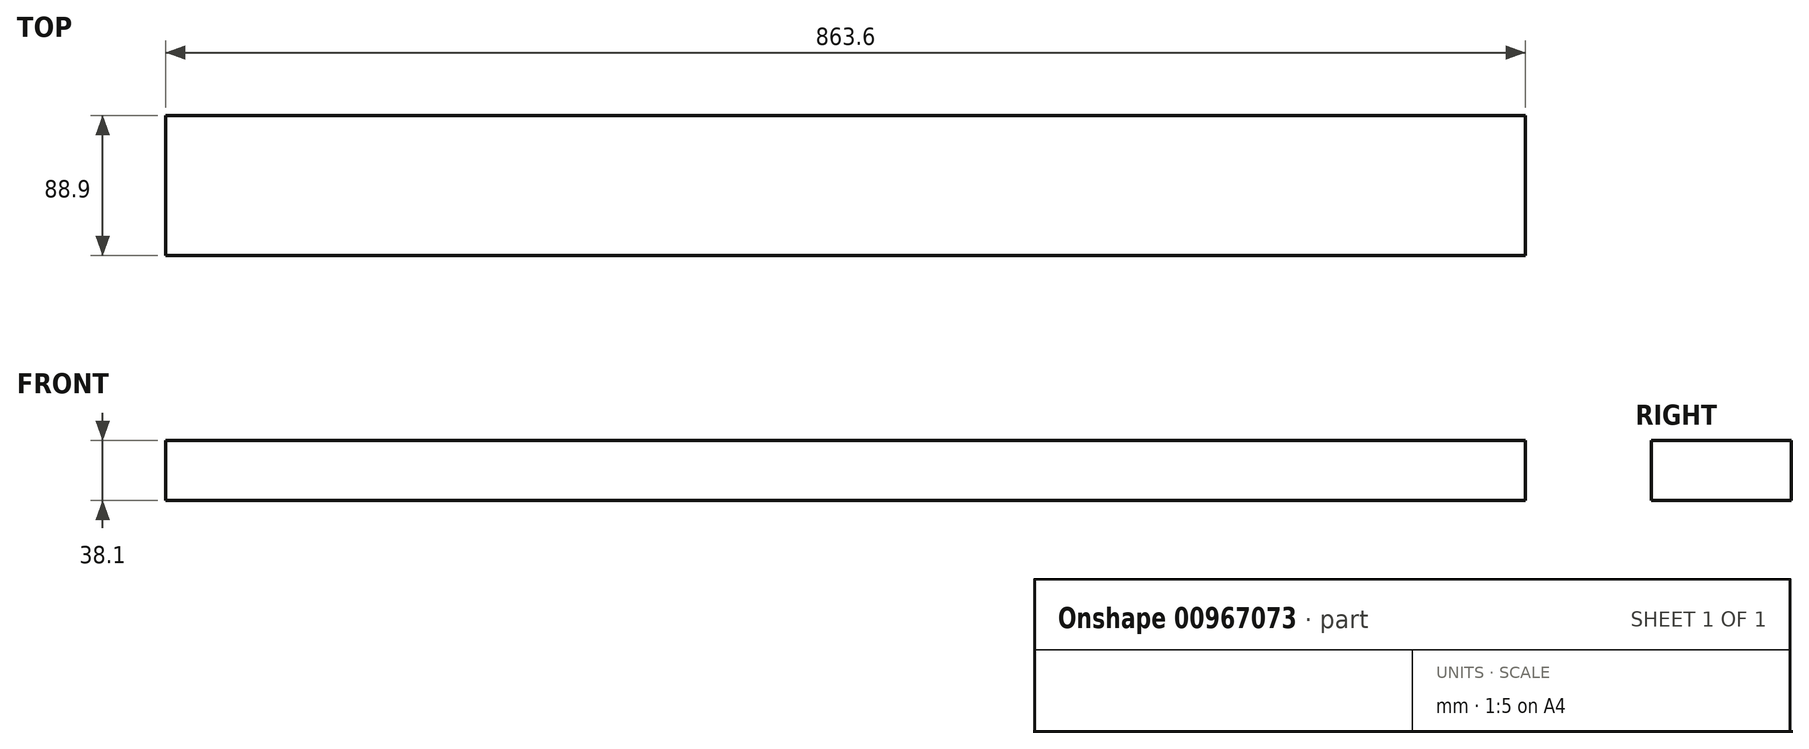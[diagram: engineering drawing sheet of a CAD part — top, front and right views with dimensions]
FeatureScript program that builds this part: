
annotation { "Feature Type Name" : "Feature", "Feature Type Description" : "" }
export const myFeature = defineFeature(function(context is Context, id is Id, definition is map)
    precondition{}
    {
        {
            var Q0;
            Q0=qCreatedBy(makeId("Right.planeOp"),FACE);
            var sketch = newSketch(context, id + "F0", { "sketchPlane" : qUnion([Q0])});
            skLineSegment(sketch, "E0.bottom", {"start": v(0, 0) * mm, "end": v(-88.9, 0) * mm});
            skLineSegment(sketch, "E0.top", {"start": v(0, 38.1) * mm, "end": v(-88.9, 38.1) * mm});
            skLineSegment(sketch, "E0.left", {"start": v(0, 0) * mm, "end": v(0, 38.1) * mm});
            skLineSegment(sketch, "E0.right", {"start": v(-88.9, 0) * mm, "end": v(-88.9, 38.1) * mm});
            skSolve(sketch);
        }
        {
            var Q0;
            Q0=makeQuery(id+"F0.imprint","IMPRINT",FACE,{"disambiguationData":[TD([[makeQuery(id+"F0.imprint","IMPRINT",EDGE,{"derivedFrom":sQuery(id+"F0.wireOp",EDGE,"E0.bottom")}),-1.0]])]});
            extrude(context, id + "F1", {"entities" : qUnion([Q0]), "oppositeDirection" : true, "depth" : 863.6 * mm, "offsetDistance" : 25.4 * mm});
        }
    });
